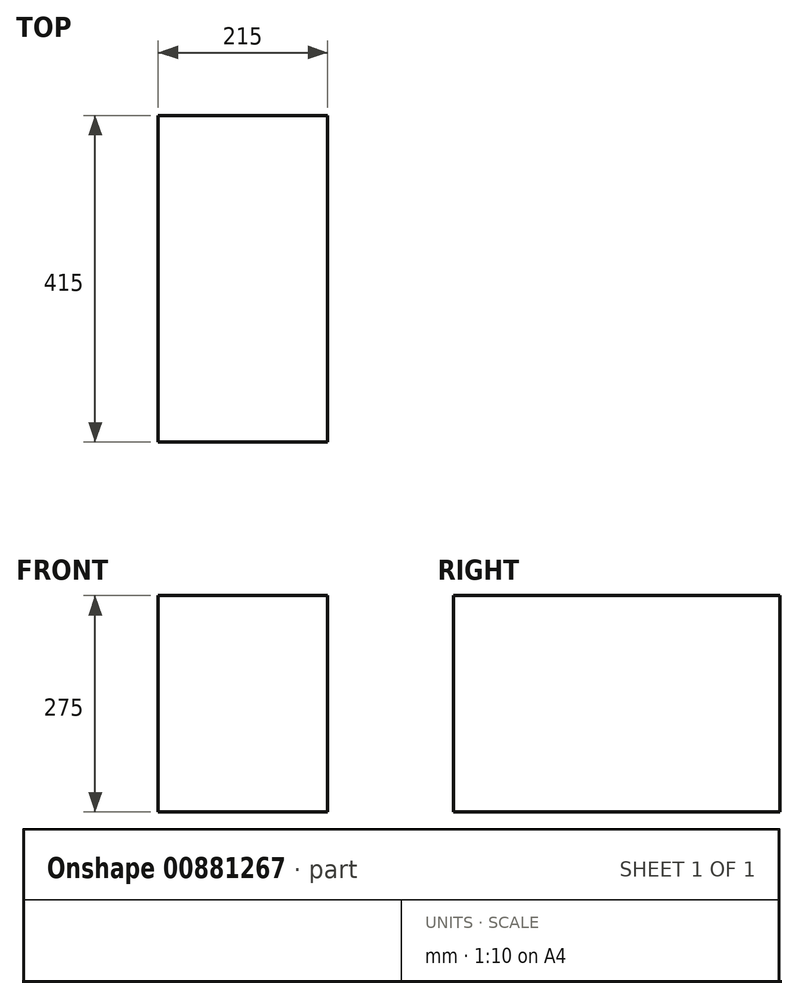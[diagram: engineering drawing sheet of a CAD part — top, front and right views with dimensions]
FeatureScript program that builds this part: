
annotation { "Feature Type Name" : "Feature", "Feature Type Description" : "" }
export const myFeature = defineFeature(function(context is Context, id is Id, definition is map)
    precondition{}
    {
        {
            var Q0;
            Q0=qCreatedBy(makeId("Front.planeOp"),FACE);
            var sketch = newSketch(context, id + "F0", { "sketchPlane" : qUnion([Q0])});
            skLineSegment(sketch, "E0.bottom", {"start": v(0, 0) * mm, "end": v(215, 0) * mm});
            skLineSegment(sketch, "E0.top", {"start": v(0, 275) * mm, "end": v(215, 275) * mm});
            skLineSegment(sketch, "E0.left", {"start": v(0, 0) * mm, "end": v(0, 275) * mm});
            skLineSegment(sketch, "E0.right", {"start": v(215, 0) * mm, "end": v(215, 275) * mm});
            skSolve(sketch);
        }
        {
            var Q0;
            Q0=makeQuery(id+"F0.imprint","IMPRINT",FACE,{"disambiguationData":[TD([[makeQuery(id+"F0.imprint","IMPRINT",EDGE,{"derivedFrom":sQuery(id+"F0.wireOp",EDGE,"E0.bottom")}),1.0]])]});
            extrude(context, id + "F1", {"entities" : qUnion([Q0]), "endBound" : BoundingType.SYMMETRIC, "depth" : 415 * mm, "offsetDistance" : 25 * mm});
        }
    });
